# Revit family: PFX_A3-Shower-Base&Enclosure-Rounded-Corner
name_source: partatom
category: Plumbing Fixtures
revit_build: Autodesk Revit 2016 (Build: 20150220_1215(x64)
units: mm (PartAtom-declared; Revit-internal decimal feet)

## family parameters
Always vertical = Yes
Cut with Voids When Loaded = No
Part Type = Undefined
Room Calculation Point = No
Round Connector Dimension = Use Diameter
Shared = No
Work Plane-Based = No

## types (4) — shared parameters
Finish = Plastic - White, Smooth

## per-type parameters (varying)
| type | Assembly Code | Depth | Side Offset | Width |
| Shower Base & Enclosure 44" x 44" | C1030220 | 3' - 8" | 1' - 10" | 3' - 8" |
| Shower Base & Enclosure 48" x 48" | C1030220 | 4' - 0" | 1' - 10" | 4' - 0" |
| Shower Base & Enclosure 36" x 36" | C1030220 | 3' - 0" | 1' - 6" | 3' - 0" |
| Shower Base & Enclosure 900 x 900mm |  | 2' - 11 7/16" | 1' - 5 23/32" | 2' - 11 7/16" |

## geometry (parser evidence)
native form markers: Sweep x1
no freeform markers — native parametric forms only
